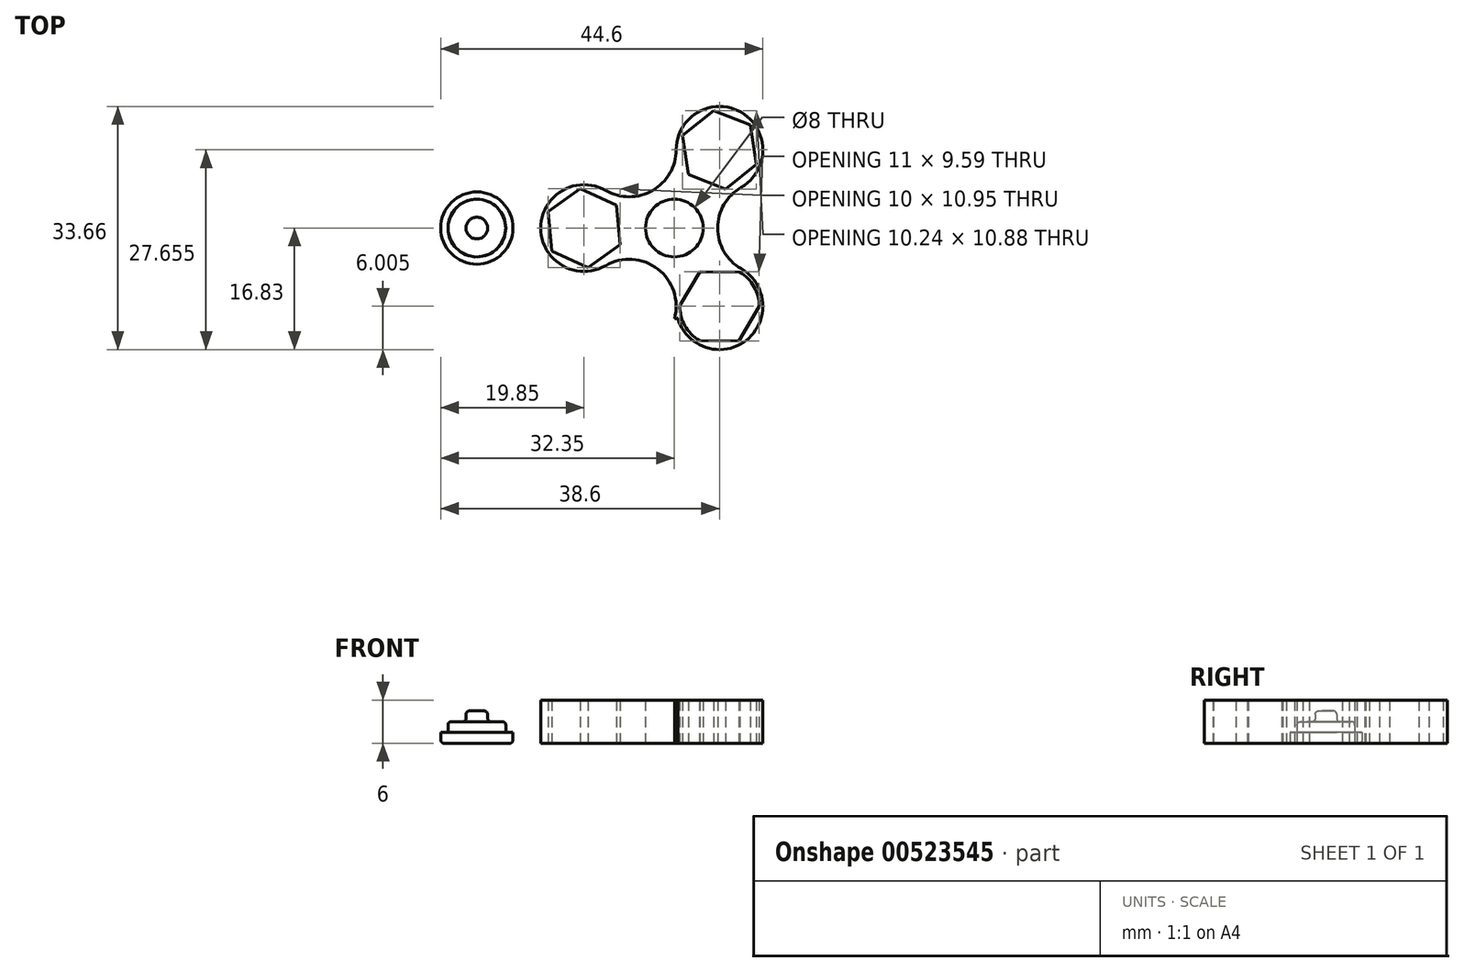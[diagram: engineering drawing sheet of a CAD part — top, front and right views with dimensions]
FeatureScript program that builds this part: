
annotation { "Feature Type Name" : "Feature", "Feature Type Description" : "" }
export const myFeature = defineFeature(function(context is Context, id is Id, definition is map)
    precondition{}
    {
        {
            var Q0;
            Q0=qCreatedBy(makeId("Top.planeOp"),FACE);
            var sketch = newSketch(context, id + "F0", { "sketchPlane" : qUnion([Q0])});
            skCircle(sketch, "E0", {"center": v(0, 0) * mm, "radius": 12.5 * mm});
            skCircle(sketch, "E1", {"center": v(0, 0) * mm, "radius": 4 * mm});
            skCircle(sketch, "E2", {"center": v(0, 0) * mm, "radius": 1.5 * mm});
            skCircle(sketch, "E3", {"center": v(-12.5, 0) * mm, "radius": 6 * mm});
            skCircle(sketch, "E4", {"center": v(6.25, 10.83) * mm, "radius": 6 * mm});
            skCircle(sketch, "E5", {"center": v(6.25, -10.83) * mm, "radius": 6 * mm});
            skArc(sketch, "E6", {"start": v(0.03, -12.5) * mm, "mid": v(-3, -5.2) * mm, "end": v(-10.84, -6.22) * mm});
            skArc(sketch, "E7", {"start": v(-10.84, 6.22) * mm, "mid": v(-3, 5.2) * mm, "end": v(0.03, 12.5) * mm});
            skArc(sketch, "E8", {"start": v(10.81, 6.28) * mm, "mid": v(6, 0) * mm, "end": v(10.8, -6.28) * mm});
            skCircle(sketch, "E9.cCircle", {"center": v(-12.5, 0) * mm, "radius": 5.5 * mm, "construction": true});
            skLineSegment(sketch, "E9.0", {"start": v(-16.98, -3.18) * mm, "end": v(-17.5, 2.3) * mm});
            skLineSegment(sketch, "E9.1", {"start": v(-17.5, 2.3) * mm, "end": v(-13.01, 5.48) * mm});
            skLineSegment(sketch, "E9.2", {"start": v(-13.01, 5.48) * mm, "end": v(-8.02, 3.18) * mm});
            skLineSegment(sketch, "E9.3", {"start": v(-8.02, 3.18) * mm, "end": v(-7.5, -2.3) * mm});
            skLineSegment(sketch, "E9.4", {"start": v(-7.5, -2.3) * mm, "end": v(-11.99, -5.48) * mm});
            skLineSegment(sketch, "E9.5", {"start": v(-11.99, -5.48) * mm, "end": v(-16.98, -3.18) * mm});
            skPoint(sketch, "E10", {"position": v(-14.49, -4.33) * mm});
            skPoint(sketch, "E11", {"position": v(-10.51, 4.33) * mm});
            skCircle(sketch, "E12", {"center": v(-12.5, 0) * mm, "radius": 5.5 * mm});
            skCircle(sketch, "E13", {"center": v(6.25, -10.83) * mm, "radius": 5.5 * mm});
            skCircle(sketch, "E14.cCircle", {"center": v(6.25, -10.83) * mm, "radius": 5.5 * mm, "construction": true});
            skLineSegment(sketch, "E14.0", {"start": v(3.44, -15.56) * mm, "end": v(0.75, -10.76) * mm});
            skLineSegment(sketch, "E14.1", {"start": v(0.75, -10.76) * mm, "end": v(3.56, -6.03) * mm});
            skLineSegment(sketch, "E14.2", {"start": v(3.56, -6.03) * mm, "end": v(9.06, -6.1) * mm});
            skLineSegment(sketch, "E14.3", {"start": v(9.06, -6.1) * mm, "end": v(11.75, -10.89) * mm});
            skLineSegment(sketch, "E14.4", {"start": v(11.75, -10.89) * mm, "end": v(8.94, -15.62) * mm});
            skLineSegment(sketch, "E14.5", {"start": v(8.94, -15.62) * mm, "end": v(3.44, -15.56) * mm});
            skCircle(sketch, "E15", {"center": v(6.25, 10.83) * mm, "radius": 5.5 * mm});
            skCircle(sketch, "E16.cCircle", {"center": v(6.25, 10.83) * mm, "radius": 5.5 * mm, "construction": true});
            skLineSegment(sketch, "E16.0", {"start": v(7.07, 5.39) * mm, "end": v(1.95, 7.4) * mm});
            skLineSegment(sketch, "E16.1", {"start": v(1.95, 7.4) * mm, "end": v(1.13, 12.84) * mm});
            skLineSegment(sketch, "E16.2", {"start": v(1.13, 12.84) * mm, "end": v(5.43, 16.26) * mm});
            skLineSegment(sketch, "E16.3", {"start": v(5.43, 16.26) * mm, "end": v(10.55, 14.25) * mm});
            skLineSegment(sketch, "E16.4", {"start": v(10.55, 14.25) * mm, "end": v(11.37, 8.81) * mm});
            skLineSegment(sketch, "E16.5", {"start": v(11.37, 8.81) * mm, "end": v(7.07, 5.39) * mm});
            skSolve(sketch);
        }
        {
            var Q0;
            Q0=makeQuery(id+"F0.imprint","IMPRINT",FACE,{"disambiguationData":[TD([[makeQuery(id+"F0.imprint","IMPRINT",EDGE,{"derivedFrom":sQuery(id+"F0.wireOp",EDGE,"E1")}),-1.0]])]});
            extrude(context, id + "F1", {"entities" : qUnion([Q0]), "depth" : 6 * mm, "offsetDistance" : 25 * mm});
        }
        {
            var Q0;
            {var subQ0=sQuery(id+"F0.wireOp",EDGE,"E0");var subQ1=sQuery(id+"F0.wireOp",EDGE,"f1c7854a-6569-4da2-8000-6e541ed49c6d.2.1");var subQ2=makeQuery(id+"F0.imprint","INTERSECT",VERTEX,{"disambiguationData":[OD(0.0)],"derivedFrom":[subQ1,subQ0]});Q0=makeQuery(id+"F0.imprint","IMPRINT",FACE,{"disambiguationData":[TD([[makeQuery(id+"F0.imprint","IMPRINT",EDGE,{"disambiguationData":[TD([[subQ2,1.0]])],"derivedFrom":subQ1}),-1.0]])]});}
            var Q1;
            {var subQ1=sQuery(id+"F0.wireOp",EDGE,"E0");var subQ5=sQuery(id+"F0.wireOp",EDGE,"f1c7854a-6569-4da2-8000-6e541ed49c6d.2.1");var subQ7=makeQuery(id+"F0.imprint","INTERSECT",VERTEX,{"disambiguationData":[OD(0.0)],"derivedFrom":[subQ5,subQ1]});Q1=makeQuery(id+"F0.imprint","IMPRINT",FACE,{"disambiguationData":[TD([[makeQuery(id+"F0.imprint","IMPRINT",EDGE,{"disambiguationData":[TD([[subQ7,-1.0]])],"derivedFrom":subQ5}),-1.0]])]});}
            var Q2;
            {var subQ1=sQuery(id+"F0.wireOp",EDGE,"E0");var subQ3=sQuery(id+"F0.wireOp",EDGE,"f1c7854a-6569-4da2-8000-6e541ed49c6d.4.1");var subQ7=makeQuery(id+"F0.imprint","INTERSECT",VERTEX,{"disambiguationData":[OD(0.0)],"derivedFrom":[subQ3,subQ1]});Q2=makeQuery(id+"F0.imprint","IMPRINT",FACE,{"disambiguationData":[TD([[makeQuery(id+"F0.imprint","IMPRINT",EDGE,{"disambiguationData":[TD([[subQ7,1.0]])],"derivedFrom":subQ3}),-1.0]])]});}
            var Q3;
            {var subQ0=sQuery(id+"F0.wireOp",EDGE,"E0");var subQ1=sQuery(id+"F0.wireOp",EDGE,"f1c7854a-6569-4da2-8000-6e541ed49c6d.4.1");var subQ2=makeQuery(id+"F0.imprint","INTERSECT",VERTEX,{"disambiguationData":[OD(0.0)],"derivedFrom":[subQ1,subQ0]});Q3=makeQuery(id+"F0.imprint","IMPRINT",FACE,{"disambiguationData":[TD([[makeQuery(id+"F0.imprint","IMPRINT",EDGE,{"disambiguationData":[TD([[subQ2,-1.0]])],"derivedFrom":subQ1}),-1.0]])]});}
            var Q4;
            {var subQ0=sQuery(id+"F0.wireOp",EDGE,"E0");var subQ1=sQuery(id+"F0.wireOp",EDGE,"XiVVu2QQ-d68u-g68W-Hexb-vInAHnOKca7Q");var subQ2=makeQuery(id+"F0.imprint","INTERSECT",VERTEX,{"disambiguationData":[OD(0.0)],"derivedFrom":[subQ1,subQ0]});Q4=makeQuery(id+"F0.imprint","IMPRINT",FACE,{"disambiguationData":[TD([[makeQuery(id+"F0.imprint","IMPRINT",EDGE,{"disambiguationData":[TD([[subQ2,-1.0]])],"derivedFrom":subQ1}),-1.0]])]});}
            var Q5;
            {var subQ1=sQuery(id+"F0.wireOp",EDGE,"E0");var subQ3=sQuery(id+"F0.wireOp",EDGE,"XiVVu2QQ-d68u-g68W-Hexb-vInAHnOKca7Q");var subQ8=makeQuery(id+"F0.imprint","INTERSECT",VERTEX,{"disambiguationData":[OD(0.0)],"derivedFrom":[subQ3,subQ1]});Q5=makeQuery(id+"F0.imprint","IMPRINT",FACE,{"disambiguationData":[TD([[makeQuery(id+"F0.imprint","IMPRINT",EDGE,{"disambiguationData":[TD([[subQ8,1.0]])],"derivedFrom":subQ3}),-1.0]])]});}
            var Q6;
            {var subQ0=sQuery(id+"F0.wireOp",EDGE,"E9.5");Q6=makeQuery(id+"F0.imprint","IMPRINT",FACE,{"disambiguationData":[TD([[makeQuery(id+"F0.imprint","IMPRINT",EDGE,{"derivedFrom":subQ0}),1.0]])]});}
            var Q7;
            {var subQ0=sQuery(id+"F0.wireOp",EDGE,"E9.4");var subQ1=sQuery(id+"F0.wireOp",EDGE,"E0");var subQ2=makeQuery(id+"F0.imprint","INTERSECT",VERTEX,{"derivedFrom":[subQ1,subQ0]});Q7=makeQuery(id+"F0.imprint","IMPRINT",FACE,{"disambiguationData":[TD([[makeQuery(id+"F0.imprint","IMPRINT",EDGE,{"disambiguationData":[TD([[subQ2,-1.0]])],"derivedFrom":subQ1}),1.0]])]});}
            var Q8;
            {var subQ3=sQuery(id+"F0.wireOp",EDGE,"E0");var subQ5=sQuery(id+"F0.wireOp",EDGE,"E3");var subQ6=makeQuery(id+"F0.imprint","INTERSECT",VERTEX,{"disambiguationData":[OD(0.0)],"derivedFrom":[subQ3,subQ5]});Q8=makeQuery(id+"F0.imprint","IMPRINT",FACE,{"disambiguationData":[TD([[makeQuery(id+"F0.imprint","IMPRINT",EDGE,{"disambiguationData":[TD([[subQ6,-1.0]])],"derivedFrom":subQ3}),-1.0]])]});}
            var Q9;
            {var subQ0=sQuery(id+"F0.wireOp",EDGE,"E3");var subQ1=sQuery(id+"F0.wireOp",EDGE,"E0");var subQ2=makeQuery(id+"F0.imprint","INTERSECT",VERTEX,{"disambiguationData":[OD(0.0)],"derivedFrom":[subQ1,subQ0]});Q9=makeQuery(id+"F0.imprint","IMPRINT",FACE,{"disambiguationData":[TD([[makeQuery(id+"F0.imprint","IMPRINT",EDGE,{"disambiguationData":[TD([[subQ2,-1.0]])],"derivedFrom":subQ1}),1.0]])]});}
            var Q10;
            {var subQ0=sQuery(id+"F0.wireOp",EDGE,"E12");var subQ1=sQuery(id+"F0.wireOp",EDGE,"E0");var subQ2=makeQuery(id+"F0.imprint","INTERSECT",VERTEX,{"disambiguationData":[OD(0.0)],"derivedFrom":[subQ1,subQ0]});Q10=makeQuery(id+"F0.imprint","IMPRINT",FACE,{"disambiguationData":[TD([[makeQuery(id+"F0.imprint","IMPRINT",EDGE,{"disambiguationData":[TD([[subQ2,-1.0]])],"derivedFrom":subQ1}),1.0]])]});}
            var Q11;
            {var subQ0=sQuery(id+"F0.wireOp",EDGE,"E9.3");Q11=makeQuery(id+"F0.imprint","IMPRINT",FACE,{"disambiguationData":[TD([[makeQuery(id+"F0.imprint","IMPRINT",EDGE,{"derivedFrom":subQ0}),1.0]])]});}
            var Q12;
            {var subQ0=sQuery(id+"F0.wireOp",EDGE,"E9.1");Q12=makeQuery(id+"F0.imprint","IMPRINT",FACE,{"disambiguationData":[TD([[makeQuery(id+"F0.imprint","IMPRINT",EDGE,{"derivedFrom":subQ0}),1.0]])]});}
            var Q13;
            {var subQ0=sQuery(id+"F0.wireOp",EDGE,"E12");var subQ1=sQuery(id+"F0.wireOp",EDGE,"E0");var subQ2=makeQuery(id+"F0.imprint","INTERSECT",VERTEX,{"disambiguationData":[OD(0.0)],"derivedFrom":[subQ1,subQ0]});Q13=makeQuery(id+"F0.imprint","IMPRINT",FACE,{"disambiguationData":[TD([[makeQuery(id+"F0.imprint","IMPRINT",EDGE,{"disambiguationData":[TD([[subQ2,-1.0]])],"derivedFrom":subQ1}),-1.0]])]});}
            var Q14;
            {var subQ0=sQuery(id+"F0.wireOp",EDGE,"E9.0");Q14=makeQuery(id+"F0.imprint","IMPRINT",FACE,{"disambiguationData":[TD([[makeQuery(id+"F0.imprint","IMPRINT",EDGE,{"derivedFrom":subQ0}),1.0]])]});}
            var Q15;
            {var subQ0=sQuery(id+"F0.wireOp",EDGE,"E9.4");var subQ1=sQuery(id+"F0.wireOp",EDGE,"E0");var subQ2=makeQuery(id+"F0.imprint","INTERSECT",VERTEX,{"derivedFrom":[subQ1,subQ0]});Q15=makeQuery(id+"F0.imprint","IMPRINT",FACE,{"disambiguationData":[TD([[makeQuery(id+"F0.imprint","IMPRINT",EDGE,{"disambiguationData":[TD([[subQ2,-1.0]])],"derivedFrom":subQ1}),-1.0]])]});}
            var Q16;
            {var subQ3=sQuery(id+"F0.wireOp",EDGE,"E0");var subQ5=sQuery(id+"F0.wireOp",EDGE,"E5");var subQ6=makeQuery(id+"F0.imprint","INTERSECT",VERTEX,{"disambiguationData":[OD(0.0)],"derivedFrom":[subQ3,subQ5]});Q16=makeQuery(id+"F0.imprint","IMPRINT",FACE,{"disambiguationData":[TD([[makeQuery(id+"F0.imprint","IMPRINT",EDGE,{"disambiguationData":[TD([[subQ6,1.0]])],"derivedFrom":subQ3}),-1.0]])]});}
            var Q17;
            {var subQ0=sQuery(id+"F0.wireOp",EDGE,"E5");var subQ3=sQuery(id+"F0.wireOp",EDGE,"E0");var subQ4=makeQuery(id+"F0.imprint","INTERSECT",VERTEX,{"disambiguationData":[OD(0.0)],"derivedFrom":[subQ3,subQ0]});Q17=makeQuery(id+"F0.imprint","IMPRINT",FACE,{"disambiguationData":[TD([[makeQuery(id+"F0.imprint","IMPRINT",EDGE,{"disambiguationData":[TD([[subQ4,1.0]])],"derivedFrom":subQ3}),1.0]])]});}
            var Q18;
            {var subQ0=sQuery(id+"F0.wireOp",EDGE,"E13");var subQ1=sQuery(id+"F0.wireOp",EDGE,"E0");var subQ2=makeQuery(id+"F0.imprint","INTERSECT",VERTEX,{"disambiguationData":[OD(1.0)],"derivedFrom":[subQ1,subQ0]});Q18=makeQuery(id+"F0.imprint","IMPRINT",FACE,{"disambiguationData":[TD([[makeQuery(id+"F0.imprint","IMPRINT",EDGE,{"disambiguationData":[TD([[subQ2,-1.0]])],"derivedFrom":subQ1}),-1.0]])]});}
            var Q19;
            {var subQ0=sQuery(id+"F0.wireOp",EDGE,"E14.5");Q19=makeQuery(id+"F0.imprint","IMPRINT",FACE,{"disambiguationData":[TD([[makeQuery(id+"F0.imprint","IMPRINT",EDGE,{"derivedFrom":subQ0}),1.0]])]});}
            var Q20;
            {var subQ0=sQuery(id+"F0.wireOp",EDGE,"E14.4");Q20=makeQuery(id+"F0.imprint","IMPRINT",FACE,{"disambiguationData":[TD([[makeQuery(id+"F0.imprint","IMPRINT",EDGE,{"derivedFrom":subQ0}),1.0]])]});}
            var Q21;
            {var subQ0=sQuery(id+"F0.wireOp",EDGE,"E13");var subQ1=sQuery(id+"F0.wireOp",EDGE,"E0");var subQ2=makeQuery(id+"F0.imprint","INTERSECT",VERTEX,{"disambiguationData":[OD(0.0)],"derivedFrom":[subQ1,subQ0]});Q21=makeQuery(id+"F0.imprint","IMPRINT",FACE,{"disambiguationData":[TD([[makeQuery(id+"F0.imprint","IMPRINT",EDGE,{"disambiguationData":[TD([[subQ2,1.0]])],"derivedFrom":subQ1}),-1.0]])]});}
            var Q22;
            {var subQ0=sQuery(id+"F0.wireOp",EDGE,"E14.2");Q22=makeQuery(id+"F0.imprint","IMPRINT",FACE,{"disambiguationData":[TD([[makeQuery(id+"F0.imprint","IMPRINT",EDGE,{"derivedFrom":subQ0}),1.0]])]});}
            var Q23;
            {var subQ0=sQuery(id+"F0.wireOp",EDGE,"E14.1");Q23=makeQuery(id+"F0.imprint","IMPRINT",FACE,{"disambiguationData":[TD([[makeQuery(id+"F0.imprint","IMPRINT",EDGE,{"derivedFrom":subQ0}),1.0]])]});}
            var Q24;
            {var subQ0=sQuery(id+"F0.wireOp",EDGE,"E13");var subQ1=sQuery(id+"F0.wireOp",EDGE,"E0");var subQ2=makeQuery(id+"F0.imprint","INTERSECT",VERTEX,{"disambiguationData":[OD(1.0)],"derivedFrom":[subQ1,subQ0]});Q24=makeQuery(id+"F0.imprint","IMPRINT",FACE,{"disambiguationData":[TD([[makeQuery(id+"F0.imprint","IMPRINT",EDGE,{"disambiguationData":[TD([[subQ2,-1.0]])],"derivedFrom":subQ1}),1.0]])]});}
            var Q25;
            {var subQ0=sQuery(id+"F0.wireOp",EDGE,"E13");var subQ1=sQuery(id+"F0.wireOp",EDGE,"E0");var subQ2=makeQuery(id+"F0.imprint","INTERSECT",VERTEX,{"disambiguationData":[OD(0.0)],"derivedFrom":[subQ1,subQ0]});Q25=makeQuery(id+"F0.imprint","IMPRINT",FACE,{"disambiguationData":[TD([[makeQuery(id+"F0.imprint","IMPRINT",EDGE,{"disambiguationData":[TD([[subQ2,1.0]])],"derivedFrom":subQ1}),1.0]])]});}
            var Q26;
            {var subQ0=sQuery(id+"F0.wireOp",EDGE,"E4");var subQ3=sQuery(id+"F0.wireOp",EDGE,"E0");var subQ7=makeQuery(id+"F0.imprint","INTERSECT",VERTEX,{"disambiguationData":[OD(0.0)],"derivedFrom":[subQ3,subQ0]});Q26=makeQuery(id+"F0.imprint","IMPRINT",FACE,{"disambiguationData":[TD([[makeQuery(id+"F0.imprint","IMPRINT",EDGE,{"disambiguationData":[TD([[subQ7,-1.0]])],"derivedFrom":subQ3}),1.0]])]});}
            var Q27;
            {var subQ0=sQuery(id+"F0.wireOp",EDGE,"E4");var subQ1=sQuery(id+"F0.wireOp",EDGE,"E0");var subQ2=makeQuery(id+"F0.imprint","INTERSECT",VERTEX,{"disambiguationData":[OD(0.0)],"derivedFrom":[subQ1,subQ0]});Q27=makeQuery(id+"F0.imprint","IMPRINT",FACE,{"disambiguationData":[TD([[makeQuery(id+"F0.imprint","IMPRINT",EDGE,{"disambiguationData":[TD([[subQ2,-1.0]])],"derivedFrom":subQ1}),-1.0]])]});}
            var Q28;
            {var subQ0=sQuery(id+"F0.wireOp",EDGE,"E16.1");var subQ1=sQuery(id+"F0.wireOp",EDGE,"E0");var subQ2=makeQuery(id+"F0.imprint","INTERSECT",VERTEX,{"derivedFrom":[subQ1,subQ0]});Q28=makeQuery(id+"F0.imprint","IMPRINT",FACE,{"disambiguationData":[TD([[makeQuery(id+"F0.imprint","IMPRINT",EDGE,{"disambiguationData":[TD([[subQ2,-1.0]])],"derivedFrom":subQ1}),1.0]])]});}
            var Q29;
            {var subQ0=sQuery(id+"F0.wireOp",EDGE,"E16.0");Q29=makeQuery(id+"F0.imprint","IMPRINT",FACE,{"disambiguationData":[TD([[makeQuery(id+"F0.imprint","IMPRINT",EDGE,{"derivedFrom":subQ0}),1.0]])]});}
            var Q30;
            {var subQ0=sQuery(id+"F0.wireOp",EDGE,"E15");var subQ1=sQuery(id+"F0.wireOp",EDGE,"E0");var subQ2=makeQuery(id+"F0.imprint","INTERSECT",VERTEX,{"disambiguationData":[OD(0.0)],"derivedFrom":[subQ1,subQ0]});Q30=makeQuery(id+"F0.imprint","IMPRINT",FACE,{"disambiguationData":[TD([[makeQuery(id+"F0.imprint","IMPRINT",EDGE,{"disambiguationData":[TD([[subQ2,-1.0]])],"derivedFrom":subQ1}),1.0]])]});}
            var Q31;
            {var subQ0=sQuery(id+"F0.wireOp",EDGE,"E15");var subQ1=sQuery(id+"F0.wireOp",EDGE,"E0");var subQ2=makeQuery(id+"F0.imprint","INTERSECT",VERTEX,{"disambiguationData":[OD(0.0)],"derivedFrom":[subQ1,subQ0]});Q31=makeQuery(id+"F0.imprint","IMPRINT",FACE,{"disambiguationData":[TD([[makeQuery(id+"F0.imprint","IMPRINT",EDGE,{"disambiguationData":[TD([[subQ2,-1.0]])],"derivedFrom":subQ1}),-1.0]])]});}
            var Q32;
            {var subQ0=sQuery(id+"F0.wireOp",EDGE,"E16.4");Q32=makeQuery(id+"F0.imprint","IMPRINT",FACE,{"disambiguationData":[TD([[makeQuery(id+"F0.imprint","IMPRINT",EDGE,{"derivedFrom":subQ0}),1.0]])]});}
            var Q33;
            {var subQ0=sQuery(id+"F0.wireOp",EDGE,"E16.3");Q33=makeQuery(id+"F0.imprint","IMPRINT",FACE,{"disambiguationData":[TD([[makeQuery(id+"F0.imprint","IMPRINT",EDGE,{"derivedFrom":subQ0}),1.0]])]});}
            var Q34;
            {var subQ0=sQuery(id+"F0.wireOp",EDGE,"E16.2");Q34=makeQuery(id+"F0.imprint","IMPRINT",FACE,{"disambiguationData":[TD([[makeQuery(id+"F0.imprint","IMPRINT",EDGE,{"derivedFrom":subQ0}),1.0]])]});}
            var Q35;
            {var subQ0=sQuery(id+"F0.wireOp",EDGE,"E16.1");var subQ1=sQuery(id+"F0.wireOp",EDGE,"E0");var subQ2=makeQuery(id+"F0.imprint","INTERSECT",VERTEX,{"derivedFrom":[subQ1,subQ0]});Q35=makeQuery(id+"F0.imprint","IMPRINT",FACE,{"disambiguationData":[TD([[makeQuery(id+"F0.imprint","IMPRINT",EDGE,{"disambiguationData":[TD([[subQ2,-1.0]])],"derivedFrom":subQ1}),-1.0]])]});}
            extrude(context, id + "F2", {"entities" : qUnion([Q0, Q1, Q2, Q3, Q4, Q5, Q6, Q7, Q8, Q9, Q10, Q11, Q12, Q13, Q14, Q15, Q16, Q17, Q18, Q19, Q20, Q21, Q22, Q23, Q24, Q25, Q26, Q27, Q28, Q29, Q30, Q31, Q32, Q33, Q34, Q35]), "operationType" : NewBodyOperationType.ADD, "depth" : 6 * mm, "offsetDistance" : 25 * mm});
        }
        {
            var Q0;
            Q0=qCreatedBy(makeId("Top.planeOp"),FACE);
            var sketch = newSketch(context, id + "F3", { "sketchPlane" : qUnion([Q0])});
            skCircle(sketch, "E17", {"center": v(0, 0) * mm, "radius": 4 * mm});
            skCircle(sketch, "E18", {"center": v(0, 0) * mm, "radius": 1.5 * mm});
            skSolve(sketch);
        }
        {
            var Q0;
            Q0=qCreatedBy(makeId("Top.planeOp"),FACE);
            var sketch = newSketch(context, id + "F4", { "sketchPlane" : qUnion([Q0])});
            skCircle(sketch, "E19", {"center": v(-27.35, 0) * mm, "radius": 5 * mm});
            skCircle(sketch, "E20", {"center": v(-27.35, 0) * mm, "radius": 4 * mm});
            skCircle(sketch, "E21", {"center": v(-27.35, 0) * mm, "radius": 1.5 * mm});
            skSolve(sketch);
        }
        {
            var Q0;
            Q0=makeQuery(id+"F4.imprint","IMPRINT",FACE,{"disambiguationData":[TD([[makeQuery(id+"F4.imprint","IMPRINT",EDGE,{"derivedFrom":sQuery(id+"F4.wireOp",EDGE,"E19")}),1.0]])]});
            var Q1;
            Q1=makeQuery(id+"F4.imprint","IMPRINT",FACE,{"disambiguationData":[TD([[makeQuery(id+"F4.imprint","IMPRINT",EDGE,{"derivedFrom":sQuery(id+"F4.wireOp",EDGE,"E20")}),1.0]])]});
            var Q2;
            Q2=makeQuery(id+"F4.imprint","IMPRINT",FACE,{"disambiguationData":[TD([[makeQuery(id+"F4.imprint","IMPRINT",EDGE,{"derivedFrom":sQuery(id+"F4.wireOp",EDGE,"E21")}),1.0]])]});
            extrude(context, id + "F5", {"entities" : qUnion([Q0, Q1, Q2]), "depth" : 1.5 * mm, "offsetDistance" : 25 * mm});
        }
        {
            var Q0;
            Q0=makeQuery(id+"F4.imprint","IMPRINT",FACE,{"disambiguationData":[TD([[makeQuery(id+"F4.imprint","IMPRINT",EDGE,{"derivedFrom":sQuery(id+"F4.wireOp",EDGE,"E20")}),1.0]])]});
            var Q1;
            Q1=makeQuery(id+"F4.imprint","IMPRINT",FACE,{"disambiguationData":[TD([[makeQuery(id+"F4.imprint","IMPRINT",EDGE,{"derivedFrom":sQuery(id+"F4.wireOp",EDGE,"E21")}),1.0]])]});
            extrude(context, id + "F6", {"entities" : qUnion([Q0, Q1]), "operationType" : NewBodyOperationType.ADD, "depth" : 3 * mm, "offsetDistance" : 25 * mm});
        }
        {
            var Q0;
            Q0=makeQuery(id+"F4.imprint","IMPRINT",FACE,{"disambiguationData":[TD([[makeQuery(id+"F4.imprint","IMPRINT",EDGE,{"derivedFrom":sQuery(id+"F4.wireOp",EDGE,"E21")}),1.0]])]});
            extrude(context, id + "F7", {"entities" : qUnion([Q0]), "operationType" : NewBodyOperationType.ADD, "depth" : 4.5 * mm, "offsetDistance" : 25 * mm});
        }
        {
            var Q0;
            Q0=makeQuery(id+"F6.opExtrude","CAP_FACE",FACE,{"disambiguationData":[OSD([sQuery(id+"F4.wireOp",EDGE,"E20")])],"isStart":false});
            fillet(context, id + "F8", {"entities" : qUnion([Q0]), "radius" : 0.5 * mm, "rho" : 0.5, "crossSection" : FilletCrossSection.CONIC, "allowEdgeOverflow" : false});
        }
        {
            var Q0;
            Q0=makeQuery(id+"F7.opExtrude","CAP_FACE",FACE,{"disambiguationData":[OSD([sQuery(id+"F4.wireOp",EDGE,"E21")])],"isStart":false});
            fillet(context, id + "F9", {"entities" : qUnion([Q0]), "radius" : 0.5 * mm, "tangentPropagation" : true, "allowEdgeOverflow" : false});
        }
        {
            var Q0;
            Q0=makeQuery(id+"F5.opExtrude","CAP_EDGE",EDGE,{"disambiguationData":[OSD([sQuery(id+"F4.wireOp",EDGE,"E19")])],"isStart":true});
            fillet(context, id + "F10", {"entities" : qUnion([Q0]), "radius" : 0.5 * mm, "tangentPropagation" : true, "allowEdgeOverflow" : false});
        }
    });
